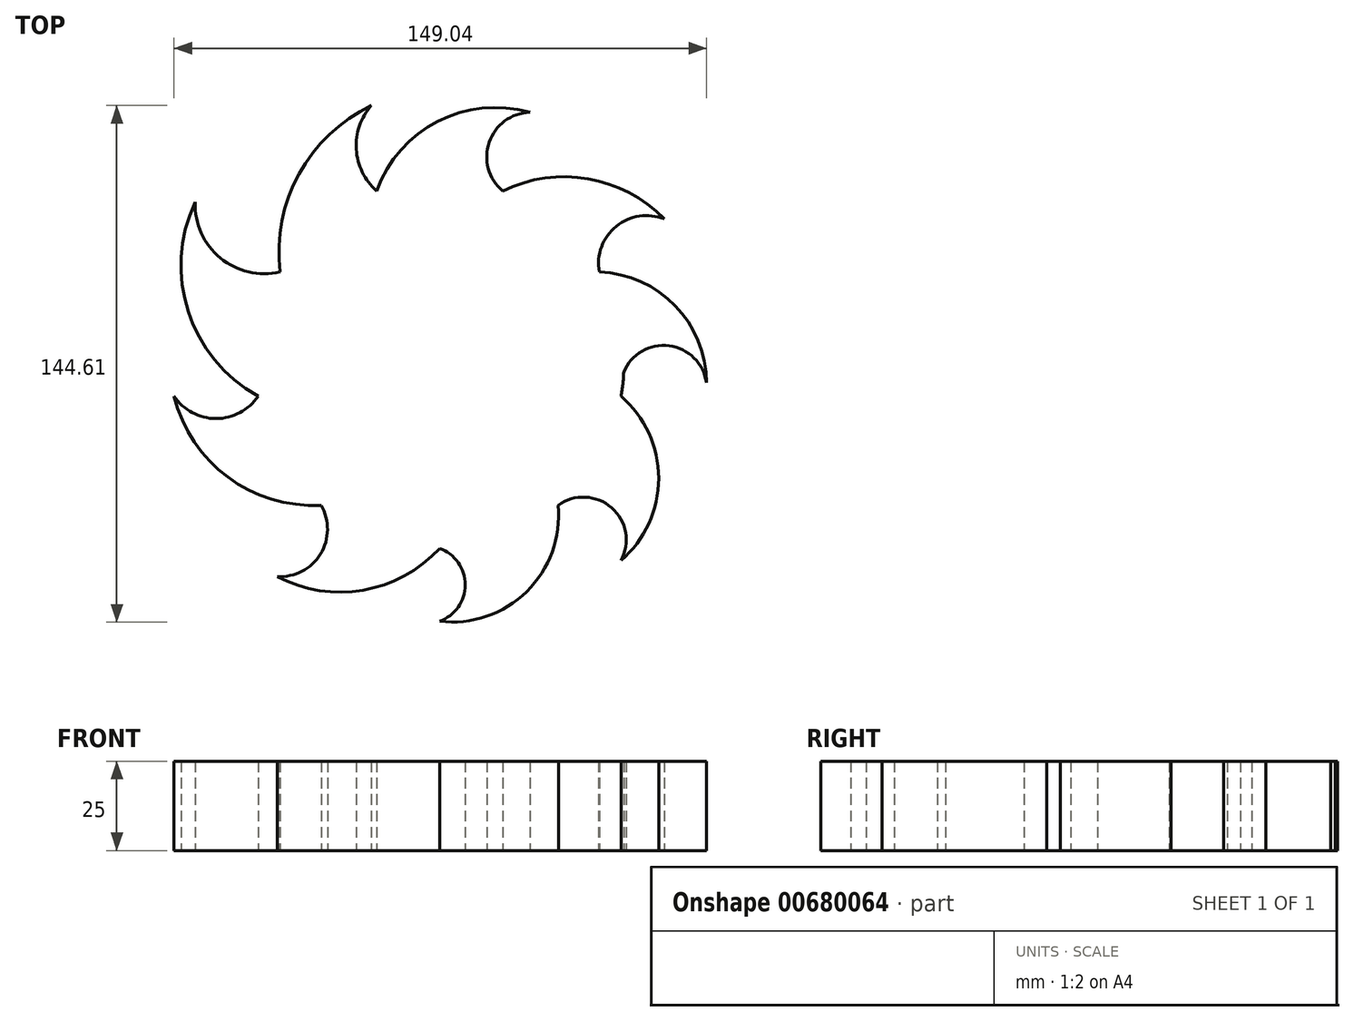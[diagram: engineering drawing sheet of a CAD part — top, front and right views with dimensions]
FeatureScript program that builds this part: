
annotation { "Feature Type Name" : "Feature", "Feature Type Description" : "" }
export const myFeature = defineFeature(function(context is Context, id is Id, definition is map)
    precondition{}
    {
        {
            var Q0;
            Q0=qCreatedBy(makeId("Top.planeOp"),FACE);
            var sketch = newSketch(context, id + "F0", { "sketchPlane" : qUnion([Q0])});
            skCircle(sketch, "E0.cCircle", {"center": v(0, 0) * mm, "radius": 48.48 * mm, "construction": true});
            skLineSegment(sketch, "E0.0", {"start": v(-17.65, 48.48) * mm, "end": v(17.65, 48.48) * mm});
            skLineSegment(sketch, "E0.1", {"start": v(17.65, 48.48) * mm, "end": v(44.68, 25.8) * mm});
            skLineSegment(sketch, "E0.2", {"start": v(44.68, 25.8) * mm, "end": v(50.81, -8.96) * mm});
            skLineSegment(sketch, "E0.3", {"start": v(50.81, -8.96) * mm, "end": v(33.16, -39.52) * mm});
            skLineSegment(sketch, "E0.4", {"start": v(33.16, -39.52) * mm, "end": v(0, -51.6) * mm});
            skLineSegment(sketch, "E0.5", {"start": v(0, -51.6) * mm, "end": v(-33.16, -39.52) * mm});
            skLineSegment(sketch, "E0.6", {"start": v(-33.16, -39.52) * mm, "end": v(-50.81, -8.96) * mm});
            skLineSegment(sketch, "E0.7", {"start": v(-50.81, -8.96) * mm, "end": v(-44.68, 25.8) * mm});
            skLineSegment(sketch, "E0.8", {"start": v(-44.68, 25.8) * mm, "end": v(-17.65, 48.48) * mm});
            skPoint(sketch, "E0.0.midPoint", {"position": v(0, 48.48) * mm});
            skCircle(sketch, "E1", {"center": v(0, 0) * mm, "radius": 51.6 * mm});
            skArc(sketch, "E2", {"start": v(25.24, 70.5) * mm, "mid": v(-0.54, 67.93) * mm, "end": v(-17.65, 48.48) * mm});
            skArc(sketch, "E3", {"start": v(25.24, 70.5) * mm, "mid": v(13.88, 62.1) * mm, "end": v(17.65, 48.48) * mm});
            skArc(sketch, "E4", {"start": v(62.9, 40.64) * mm, "mid": v(41.54, 51.86) * mm, "end": v(17.65, 48.48) * mm});
            skArc(sketch, "E5", {"start": v(62.9, 40.64) * mm, "mid": v(49.43, 38.56) * mm, "end": v(44.68, 25.8) * mm});
            skArc(sketch, "E6", {"start": v(74.7, -5.19) * mm, "mid": v(65.93, 16.35) * mm, "end": v(44.68, 25.8) * mm});
            skArc(sketch, "E7", {"start": v(74.7, -5.19) * mm, "mid": v(60.83, 5.09) * mm, "end": v(50.81, -8.96) * mm});
            skArc(sketch, "E8", {"start": v(50.81, -55) * mm, "mid": v(61.33, -31.98) * mm, "end": v(50.81, -8.96) * mm});
            skArc(sketch, "E9", {"start": v(50.81, -55) * mm, "mid": v(48.16, -40.23) * mm, "end": v(33.16, -39.52) * mm});
            skArc(sketch, "E10", {"start": v(-45.48, -59.48) * mm, "mid": v(-21.4, -63.28) * mm, "end": v(0, -51.6) * mm});
            skArc(sketch, "E11", {"start": v(-45.48, -59.48) * mm, "mid": v(-33.36, -53.18) * mm, "end": v(-33.16, -39.52) * mm});
            skArc(sketch, "E12", {"start": v(-74.34, -8.96) * mm, "mid": v(-59.24, -31.64) * mm, "end": v(-33.16, -39.52) * mm});
            skArc(sketch, "E13", {"start": v(-74.34, -8.96) * mm, "mid": v(-62.58, -15.25) * mm, "end": v(-50.81, -8.96) * mm});
            skArc(sketch, "E14", {"start": v(-19.1, 72.4) * mm, "mid": v(-39.4, 53.22) * mm, "end": v(-44.68, 25.8) * mm});
            skArc(sketch, "E15", {"start": v(-19.1, 72.4) * mm, "mid": v(-23.33, 60.14) * mm, "end": v(-17.65, 48.48) * mm});
            skArc(sketch, "E16", {"start": v(-68.42, 45.33) * mm, "mid": v(-70.36, 14.7) * mm, "end": v(-50.81, -8.96) * mm});
            skArc(sketch, "E17", {"start": v(-68.42, 45.33) * mm, "mid": v(-61.37, 29.7) * mm, "end": v(-44.68, 25.8) * mm});
            skArc(sketch, "E18", {"start": v(0, -72) * mm, "mid": v(24.36, -63.7) * mm, "end": v(33.16, -39.52) * mm});
            skArc(sketch, "E19", {"start": v(0, -72) * mm, "mid": v(7.15, -61.8) * mm, "end": v(0, -51.6) * mm});
            skSolve(sketch);
        }
        {
            var Q0;
            Q0 = qSketchRegion(id + "F0", true);
            extrude(context, id + "F1", {"entities" : qUnion([Q0]), "depth" : 25 * mm, "offsetDistance" : 25 * mm});
        }
    });
